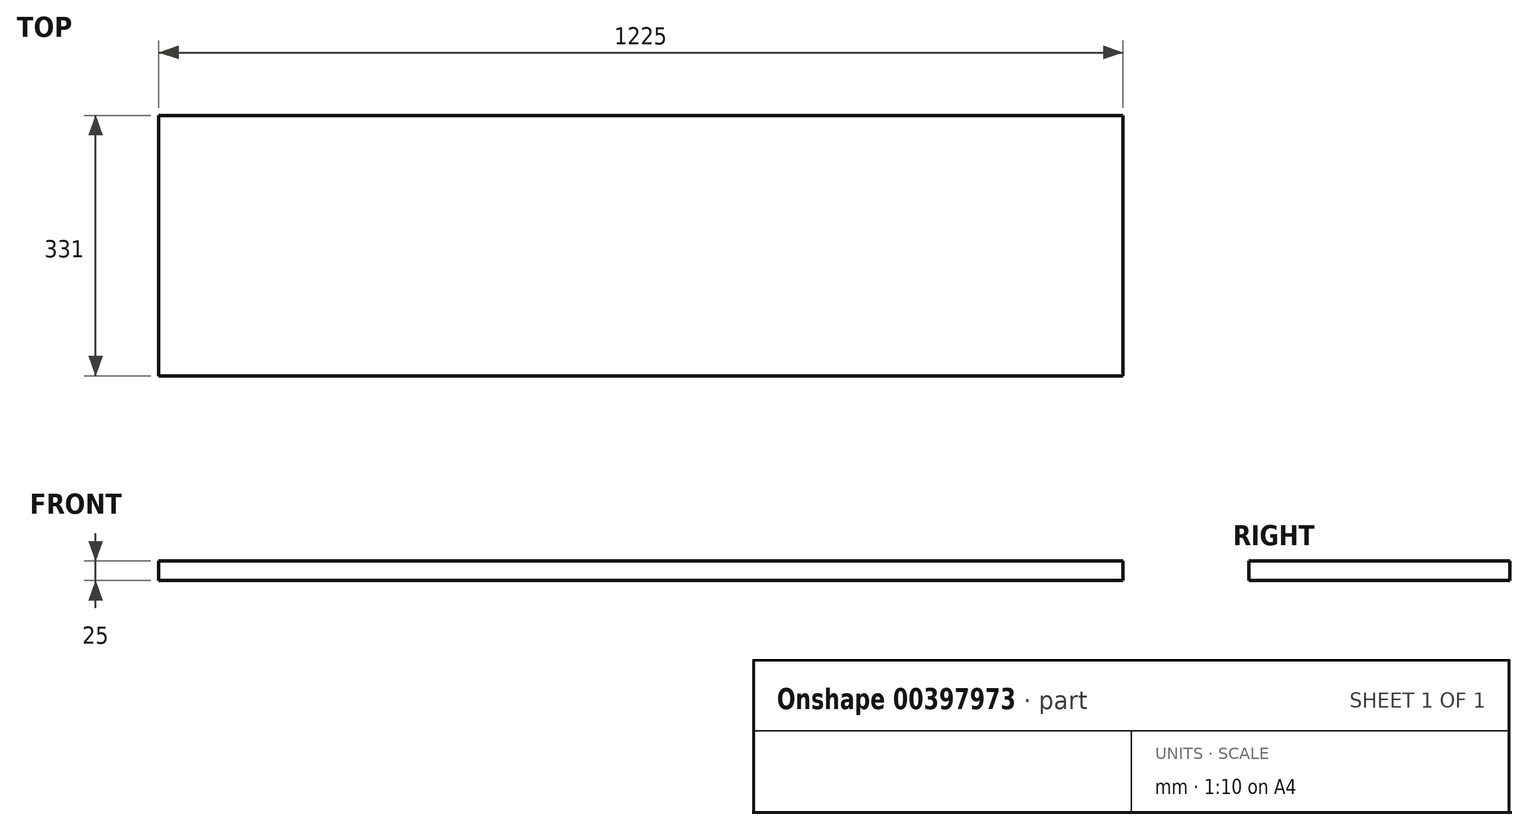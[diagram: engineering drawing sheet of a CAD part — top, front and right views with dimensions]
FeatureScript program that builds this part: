
annotation { "Feature Type Name" : "Feature", "Feature Type Description" : "" }
export const myFeature = defineFeature(function(context is Context, id is Id, definition is map)
    precondition{}
    {
        {
            var Q0;
            Q0=qCreatedBy(makeId("Front.planeOp"),FACE);
            var sketch = newSketch(context, id + "F0", { "sketchPlane" : qUnion([Q0])});
            skLineSegment(sketch, "E0.bottom", {"start": v(-612.5, 12.5) * mm, "end": v(612.5, 12.5) * mm});
            skLineSegment(sketch, "E0.top", {"start": v(-612.5, -12.5) * mm, "end": v(612.5, -12.5) * mm});
            skLineSegment(sketch, "E0.left", {"start": v(-612.5, 12.5) * mm, "end": v(-612.5, -12.5) * mm});
            skLineSegment(sketch, "E0.right", {"start": v(612.5, 12.5) * mm, "end": v(612.5, -12.5) * mm});
            skLineSegment(sketch, "E1", {"start": v(0, 12.5) * mm, "end": v(0, -12.5) * mm, "construction": true});
            skSolve(sketch);
        }
        {
            var Q0;
            Q0=makeQuery(id+"F0.imprint","IMPRINT",FACE,{"disambiguationData":[TD([[makeQuery(id+"F0.imprint","IMPRINT",EDGE,{"derivedFrom":sQuery(id+"F0.wireOp",EDGE,"E0.bottom")}),-1.0]])]});
            extrude(context, id + "F1", {"entities" : qUnion([Q0]), "depth" : 331 * mm});
        }
    });
